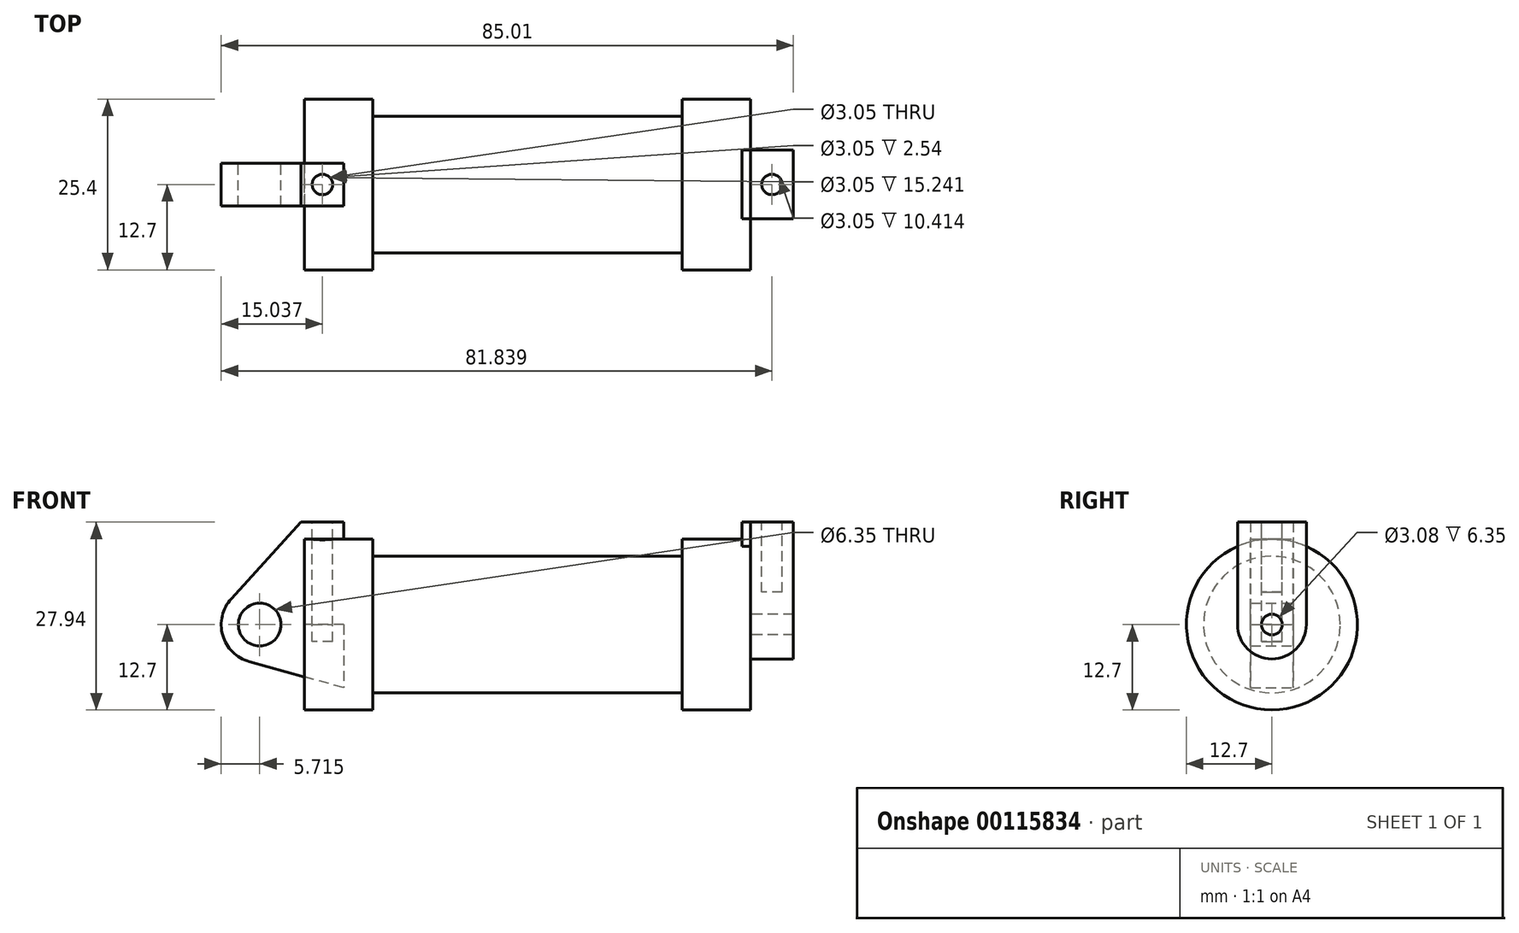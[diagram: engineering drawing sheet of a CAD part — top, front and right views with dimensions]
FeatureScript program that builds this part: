
annotation { "Feature Type Name" : "Feature", "Feature Type Description" : "" }
export const myFeature = defineFeature(function(context is Context, id is Id, definition is map)
    precondition{}
    {
        {
            var Q0;
            Q0=qCreatedBy(makeId("Front.planeOp"),FACE);
            var sketch = newSketch(context, id + "F0", { "sketchPlane" : qUnion([Q0])});
            skLineSegment(sketch, "E0", {"start": v(0, 0) * mm, "end": v(0, 12.7) * mm});
            skLineSegment(sketch, "E1", {"start": v(0, 12.7) * mm, "end": v(10.16, 12.7) * mm});
            skLineSegment(sketch, "E2", {"start": v(10.16, 12.7) * mm, "end": v(10.16, 10.16) * mm});
            skLineSegment(sketch, "E3", {"start": v(10.16, 10.16) * mm, "end": v(56.13, 10.16) * mm});
            skLineSegment(sketch, "E4", {"start": v(56.13, 10.16) * mm, "end": v(56.13, 12.7) * mm});
            skLineSegment(sketch, "E5", {"start": v(56.13, 12.7) * mm, "end": v(66.3, 12.7) * mm});
            skLineSegment(sketch, "E6", {"start": v(66.3, 12.7) * mm, "end": v(66.3, 0) * mm});
            skLineSegment(sketch, "E7", {"start": v(66.3, 0) * mm, "end": v(0, 0) * mm});
            skLineSegment(sketch, "E8", {"start": v(5.84, 15.24) * mm, "end": v(-0.5, 15.24) * mm});
            skLineSegment(sketch, "E9", {"start": v(-0.5, 15.24) * mm, "end": v(-10.88, 3.85) * mm});
            skLineSegment(sketch, "E10", {"start": v(0, 0) * mm, "end": v(-6.65, 0) * mm});
            skCircle(sketch, "E11", {"center": v(-6.65, 0) * mm, "radius": 5.72 * mm});
            skCircle(sketch, "E12", {"center": v(-6.65, 0) * mm, "radius": 3.18 * mm});
            skLineSegment(sketch, "E13", {"start": v(5.84, 15.24) * mm, "end": v(5.84, -9.4) * mm});
            skLineSegment(sketch, "E14", {"start": v(5.84, -9.4) * mm, "end": v(-8.18, -5.5) * mm});
            skSolve(sketch);
        }
        {
            var Q0;
            {var subQ0=sQuery(id+"F0.wireOp",EDGE,"E0");Q0=makeQuery(id+"F0.imprint","IMPRINT",FACE,{"disambiguationData":[TD([[makeQuery(id+"F0.imprint","IMPRINT",EDGE,{"derivedFrom":subQ0}),-1.0]])]});}
            var Q1;
            {var subQ0=sQuery(id+"F0.wireOp",EDGE,"E2");Q1=makeQuery(id+"F0.imprint","IMPRINT",FACE,{"disambiguationData":[TD([[makeQuery(id+"F0.imprint","IMPRINT",EDGE,{"derivedFrom":subQ0}),-1.0]])]});}
            var Q2;
            Q2=sQuery(id+"F0.wireOp",EDGE,"E7");
            revolve(context, id + "F1", {"entities" : qUnion([Q0, Q1]), "axis" : qUnion([Q2]), "revolveType" : RevolveType.FULL});
        }
        {
            var Q0;
            {var subQ4=sQuery(id+"F0.wireOp",EDGE,"E12");Q0=makeQuery(id+"F0.imprint","IMPRINT",FACE,{"disambiguationData":[TD([[makeQuery(id+"F0.imprint","IMPRINT",EDGE,{"derivedFrom":subQ4}),-1.0]])]});}
            var Q1;
            {var subQ0=sQuery(id+"F0.wireOp",EDGE,"E14");Q1=makeQuery(id+"F0.imprint","IMPRINT",FACE,{"disambiguationData":[TD([[makeQuery(id+"F0.imprint","IMPRINT",EDGE,{"derivedFrom":subQ0}),-1.0]])]});}
            var Q2;
            {var subQ3=sQuery(id+"F0.wireOp",EDGE,"E0");Q2=makeQuery(id+"F0.imprint","IMPRINT",FACE,{"disambiguationData":[TD([[makeQuery(id+"F0.imprint","IMPRINT",EDGE,{"derivedFrom":subQ3}),1.0]])]});}
            extrude(context, id + "F2", {"entities" : qUnion([Q0, Q1, Q2]), "endBound" : BoundingType.SYMMETRIC, "depth" : 6.35 * mm});
        }
        {
            var Q0;
            Q0=makeQuery(id+"F1.opRevolve","SWEPT_FACE",FACE,{"disambiguationData":[OSD([sQuery(id+"F0.wireOp",EDGE,"E6")])]});
            var sketch = newSketch(context, id + "F3", { "sketchPlane" : qUnion([Q0])});
            skCircle(sketch, "E15", {"center": v(0, 0) * mm, "radius": 1.54 * mm});
            skCircle(sketch, "E16", {"center": v(0, 0) * mm, "radius": 5.11 * mm});
            skLineSegment(sketch, "E17", {"start": v(5.11, 0) * mm, "end": v(5.11, 15.24) * mm});
            skLineSegment(sketch, "E18", {"start": v(-5.11, 0) * mm, "end": v(-5.11, 15.24) * mm});
            skLineSegment(sketch, "E19", {"start": v(-5.11, 15.24) * mm, "end": v(5.11, 15.24) * mm});
            skSolve(sketch);
        }
        {
            var Q0;
            Q0=makeQuery(id+"F3.imprint","IMPRINT",FACE,{"disambiguationData":[TD([[makeQuery(id+"F3.imprint","IMPRINT",EDGE,{"derivedFrom":sQuery(id+"F3.wireOp",EDGE,"E15")}),-1.0]])]});
            var Q1;
            {var subQ0=sQuery(id+"F3.wireOp",EDGE,"E17");var subQ1=sQuery(id+"F3.wireOp",EDGE,"E16");var subQ2=makeQuery(id+"F3.imprint","INTERSECT",VERTEX,{"derivedFrom":[subQ1,subQ0]});Q1=makeQuery(id+"F3.imprint","IMPRINT",FACE,{"disambiguationData":[TD([[makeQuery(id+"F3.imprint","IMPRINT",EDGE,{"disambiguationData":[TD([[subQ2,-1.0]])],"derivedFrom":subQ1}),-1.0]])]});}
            var Q2;
            {var subQ0=sQuery(id+"F3.wireOp",EDGE,"E19");Q2=makeQuery(id+"F3.imprint","IMPRINT",FACE,{"disambiguationData":[TD([[makeQuery(id+"F3.imprint","IMPRINT",EDGE,{"derivedFrom":subQ0}),-1.0]])]});}
            extrude(context, id + "F4", {"entities" : qUnion([Q0, Q1, Q2]), "operationType" : NewBodyOperationType.ADD, "depth" : 6.35 * mm});
        }
        {
            var Q0;
            Q0=makeQuery(id+"F4.opExtrude","CAP_FACE",FACE,{"disambiguationData":[OSD([sQuery(id+"F3.wireOp",EDGE,"E15"),sQuery(id+"F3.wireOp",EDGE,"E16"),sQuery(id+"F3.wireOp",EDGE,"E17"),sQuery(id+"F3.wireOp",EDGE,"E18"),sQuery(id+"F3.wireOp",EDGE,"E19")])],"isStart":true});
            extrude(context, id + "F5", {"entities" : qUnion([Q0]), "depth" : 1.27 * mm});
        }
        {
            var Q0;
            Q0=makeQuery(id+"F2.opExtrude","SWEPT_FACE",FACE,{"disambiguationData":[OSD([sQuery(id+"F0.wireOp",EDGE,"E8")])]});
            var sketch = newSketch(context, id + "F6", { "sketchPlane" : qUnion([Q0])});
            skCircle(sketch, "E20", {"center": v(2.67, 0) * mm, "radius": 1.52 * mm});
            skPoint(sketch, "E20.centerSnap0", {"position": v(2.67, 3.18) * mm});
            skPoint(sketch, "E20.centerSnap1", {"position": v(-0.5, 0) * mm});
            skSolve(sketch);
        }
        {
            var Q0;
            Q0=makeQuery(id+"F4.opExtrude","SWEPT_FACE",FACE,{"disambiguationData":[OSD([sQuery(id+"F3.wireOp",EDGE,"E19")])]});
            var sketch = newSketch(context, id + "F7", { "sketchPlane" : qUnion([Q0])});
            skCircle(sketch, "E21", {"center": v(69.47, 0) * mm, "radius": 1.52 * mm});
            skPoint(sketch, "E21.centerSnap0", {"position": v(66.3, 0) * mm});
            skPoint(sketch, "E21.centerSnap1", {"position": v(69.47, 5.11) * mm});
            skSolve(sketch);
        }
        {
            var Q0;
            Q0=makeQuery(id+"F6.imprint","IMPRINT",FACE,{"disambiguationData":[TD([[makeQuery(id+"F6.imprint","IMPRINT",EDGE,{"derivedFrom":sQuery(id+"F6.wireOp",EDGE,"E20")}),1.0]])]});
            var sketch = newSketch(context, id + "F8", { "sketchPlane" : qUnion([Q0])});
            skSolve(sketch);
        }
        {
            var Q0;
            Q0 = qSketchRegion(id + "F8", true);
            var Q1;
            Q1=makeQuery(id+"F6.imprint","IMPRINT",FACE,{"disambiguationData":[TD([[makeQuery(id+"F6.imprint","IMPRINT",EDGE,{"derivedFrom":sQuery(id+"F6.wireOp",EDGE,"E20")}),1.0]])]});
            extrude(context, id + "F9", {"entities" : qUnion([Q0, Q1]), "operationType" : NewBodyOperationType.REMOVE, "oppositeDirection" : true, "depth" : 17.78 * mm});
        }
        {
            var Q0;
            Q0=makeQuery(id+"F7.imprint","IMPRINT",FACE,{"disambiguationData":[TD([[makeQuery(id+"F7.imprint","IMPRINT",EDGE,{"derivedFrom":sQuery(id+"F7.wireOp",EDGE,"E21")}),1.0]])]});
            extrude(context, id + "F10", {"entities" : qUnion([Q0]), "operationType" : NewBodyOperationType.REMOVE, "oppositeDirection" : true, "depth" : 10.4 * mm});
        }
    });
